# Revit family: Accessory-Tissue_Holder-KOHLER-Margaux-K-16255
name_source: partatom
category: Specialty Equipment
revit_build: Autodesk Revit 2015 (Build: 20140606_1530(x64)
units: mm (PartAtom-declared; Revit-internal decimal feet)

## types (5) — shared parameters
ADA Compliant = No
Assembly Code = C1030200
Date Modified = 10/24/2018
Default Elevation = 42"
Description = Vertical Toilet Tissue Holder
Height = 7"
Length = 4 1/2"
Manufacturer = KOHLER Co.
MasterFormat 1995 = 10820
MasterFormat 2004 = 10.28.13
Material = Premium metal construction
Product Documentation Link = https://www.us.kohler.com
Product Name = Margaux
Product Page URL = https://www.us.kohler.com
URL = https://www.us.kohler.com
Width = 3"

## per-type parameters (varying)
| type | Finish | Model | Type |
| CP-Polished Chrome | Kohler-Metal-CP-Polished_Chrome | K-16255-CP | 1 |
| SN-Vibrant Polished Nickel | Kohler-Metal-SN-Vibrant_Polished_Nickel | K-16255-SN | 2 |
| AF-Vibrant French Gold | Kohler-Metal-AF-Vibrant_French_Gold | K-16255-AF | 3 |
| BN-Vibrant Brushed Nickel | Kohler-Metal-BN-Vibrant_Brushed_Nickel | K-16255-BN | 4 |
| BV-Vibrant Brushed Bronze | Kohler-Metal-BV-Brushed_Bronze | K-16255-BV | 5 |

## geometry (parser evidence)
native form markers: Sweep x3
no freeform markers — native parametric forms only
